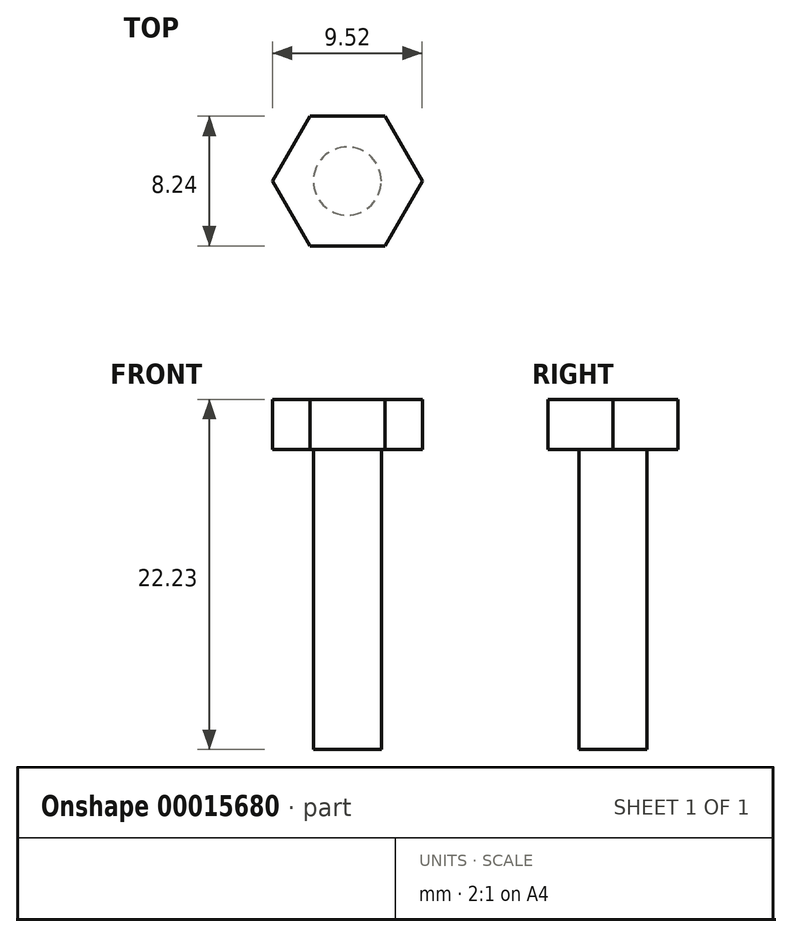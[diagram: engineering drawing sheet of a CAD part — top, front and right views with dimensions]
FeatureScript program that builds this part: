
annotation { "Feature Type Name" : "Feature", "Feature Type Description" : "" }
export const myFeature = defineFeature(function(context is Context, id is Id, definition is map)
    precondition{}
    {
        {
            var Q0;
            Q0=qCreatedBy(makeId("Top.planeOp"),FACE);
            var sketch = newSketch(context, id + "F0", { "sketchPlane" : qUnion([Q0])});
            skCircle(sketch, "E0", {"center": v(0, 0) * mm, "radius": 2.16 * mm});
            skSolve(sketch);
        }
        {
            var Q0;
            Q0 = qSketchRegion(id + "F0", true);
            extrude(context, id + "F1", {"entities" : qUnion([Q0]), "depth" : 19.05 * mm});
        }
        {
            var Q0;
            Q0=makeQuery(id+"F1.opExtrude","CAP_FACE",FACE,{"disambiguationData":[OSD([sQuery(id+"F0.wireOp",EDGE,"E0")])],"isStart":false});
            var sketch = newSketch(context, id + "F2", { "sketchPlane" : qUnion([Q0])});
            skCircle(sketch, "E1.cCircle", {"center": v(0, 0) * mm, "radius": 4.12 * mm, "construction": true});
            skLineSegment(sketch, "E1.0", {"start": v(2.38, -4.12) * mm, "end": v(-2.38, -4.12) * mm});
            skLineSegment(sketch, "E1.1", {"start": v(-2.38, -4.12) * mm, "end": v(-4.76, 0) * mm});
            skLineSegment(sketch, "E1.2", {"start": v(-4.76, 0) * mm, "end": v(-2.38, 4.12) * mm});
            skLineSegment(sketch, "E1.3", {"start": v(-2.38, 4.12) * mm, "end": v(2.38, 4.12) * mm});
            skLineSegment(sketch, "E1.4", {"start": v(2.38, 4.12) * mm, "end": v(4.76, 0) * mm});
            skLineSegment(sketch, "E1.5", {"start": v(4.76, 0) * mm, "end": v(2.38, -4.12) * mm});
            skPoint(sketch, "E1.0.midPoint", {"position": v(0, -4.12) * mm});
            skSolve(sketch);
        }
        {
            var Q0;
            Q0 = qSketchRegion(id + "F2", true);
            extrude(context, id + "F3", {"entities" : qUnion([Q0]), "operationType" : NewBodyOperationType.ADD, "depth" : 3.17 * mm});
        }
    });
